# Revit family: HOSPIVAC G EVISA
name_source: partatom
category: Equipement de génie climatique
revit_build: Autodesk Revit 2018 (Build: 20170223_1515(x64)
units: mm (PartAtom-declared; Revit-internal decimal feet)

## family parameters
Basée sur le plan de construction = Non
Classification = Pompe
Cote de connecteur circulaire = Utiliser le diamètre
Couper avec des vides une fois chargée = Non
Partagée = Non
Point de calcul de pièce = Non
Toujours verticalement = Oui
Type d'élément = Normal

## types (11) — shared parameters
BRANCHEMENT_TERRE = Oui
COS_PHI = 0.9
DOUBLE_ALIMENTATION = Non
FREQUENCE = 50 Hz
Fabricant = MIL'S
Lien espace client = https://www.mils.fr
Modèle = HOSPIVAC G EVISA
NBR_POLES = 3
NEUTRE = Non
TENSION_ALIM = 400 V

## per-type parameters (varying)
| type | DEBIT_ASPI_VIDE | DEGAG_CALORIFIQUE(kJ/h) | DESCR_ALIM_ELECT | DESCR_ASPI | DESCR_REFOUL | DIAM_ASPI_VIDE | HAUT_PPE | NIVEAU_SONORE(dB(A)) | OFFSET_LARG_PPE | OFFSET_LONG_PPE | POIDS(Kg) | PROTECTION_ELECTRIQUE | PROTEC_ELECT | PUISS_APPARENTE | PUISS_ELECT | TYPE_PPE | TYPE_SOCLE |
| a - HOSPIVAC G E25 | 28.0 m³/h | 3100 | Alimentation électrique, 4G1.5mm² | Aspiration Vide ; 28 m³/h ; G 1" FEM | Refoulement Vide ; 28 m³/h ; G 1" FEM | 25 mm  [stored 0.082021 ft] | 150 mm  [stored 0.492126 ft] | 59 | 135 mm  [stored 0.442913 ft] | 92.5 mm  [stored 0.303478 ft] | 36 mm  [stored 0.11811 ft] | 4 A | Disjoncteur courbe D - 4 A | 833 VA | 1 kW | EVISA : b - E25.R | SOCLE HOSPIVAC G EVISA : SOCLE E25/40 |
| b - HOSPIVAC G E40 | 44.0 m³/h | 4548 | Alimentation électrique, 4G1.5mm² | Aspiration Vide ; 44 m³/h ; G 1" FEM | Refoulement Vide ; 44 m³/h ; G 1" FEM | 25 mm  [stored 0.082021 ft] | 150 mm  [stored 0.492126 ft] | 58 | 135 mm  [stored 0.442913 ft] | 92.5 mm  [stored 0.303478 ft] | 40 mm  [stored 0.131234 ft] | 4 A | Disjoncteur courbe D - 4 A | 1222 VA | 1 kW | EVISA : d - E40.R | SOCLE HOSPIVAC G EVISA : SOCLE E25/40 |
| c - HOSPIVAC G E65 | 68.0 m³/h | 6200 | Alimentation électrique, 4G1.5mm² | Aspiration Vide ; 68 m³/h ; G 1"1/4 FEM | Refoulement Vide ; 68 m³/h ; G 1"1/4 FEM | 32 mm  [stored 0.104987 ft] | 150 mm  [stored 0.492126 ft] | 67 | 122.5 mm  [stored 0.401903 ft] | 175.5 mm  [stored 0.575787 ft] | 70.5 mm | 6 A | Disjoncteur courbe D - 6 A | 1667 VA | 2 kW | EVISA : e - E65.R | SOCLE HOSPIVAC G EVISA : SOCLE E65/100 |
| e - HOSPIVAC G E150 | 132.0 m³/h | 12403 | Alimentation électrique, 4G2.5mm² | Aspiration Vide ; 132 m³/h ; G 2" FEM | Refoulement Vide ; 132 m³/h ; G 2" FEM | 50 mm  [stored 0.164042 ft] | 150 mm  [stored 0.492126 ft] | 69 | 171.3 mm  [stored 0.562008 ft] | 133 mm  [stored 0.436352 ft] | 166 mm  [stored 0.544619 ft] | 10 A | Disjoncteur courbe D - 10 A | 3333 VA | 3 kW | EVISA : g - E150.R | SOCLE HOSPIVAC G EVISA : SOCLE E150/200 |
| d - HOSPIVAC G E100 | 100.0 m³/h | 9095 | Alimentation électrique, 4G1.5mm² | Aspiration Vide ; 100 m³/h ; G 1"1/4 FEM | Refoulement Vide ; 100 m³/h ; G 1"1/4 FEM | 32 mm  [stored 0.104987 ft] | 150 mm  [stored 0.492126 ft] | 67 | 122.5 mm  [stored 0.401903 ft] | 175.5 mm  [stored 0.575787 ft] | 74.5 mm  [stored 0.244423 ft] | 10 A | Disjoncteur courbe D - 10 A | 2444 VA | 2 kW | EVISA : f - E100.R | SOCLE HOSPIVAC G EVISA : SOCLE E65/100 |
| f - HOSPIVAC G E200 | 200.0 m³/h | 16537 | Alimentation électrique, 4G2.5mm² | Aspiration Vide ; 200 m³/h ; G 2" FEM | Refoulement Vide ; 200 m³/h ; G 2" FEM | 50 mm  [stored 0.164042 ft] | 150 mm  [stored 0.492126 ft] | 71 | 171.3 mm  [stored 0.562008 ft] | 133 mm  [stored 0.436352 ft] | 155 mm  [stored 0.50853 ft] | 16 A | Disjoncteur courbe D - 16 A | 4444 VA | 4 kW | EVISA : h - E200.R | SOCLE HOSPIVAC G EVISA : SOCLE E150/200 |
| g - HOSPIVAC G E300 | 300.0 m³/h | 22738 | Alimentation électrique, 4G2.5mm² | Aspiration Vide ; 300 m³/h ; G 2" FEM | Refoulement Vide ; 300 m³/h ; G 2" FEM | 50 mm  [stored 0.164042 ft] | 150 mm  [stored 0.492126 ft] | 72 | 206 mm  [stored 0.675853 ft] | 160 mm  [stored 0.524934 ft] | 194 mm  [stored 0.636483 ft] | 20 A | Disjoncteur courbe D - 20 A | 6111 VA | 6 kW | EVISA : i - E300.R | SOCLE HOSPIVAC G EVISA : SOCLE E300 |
| h - HOSPIVAC G E350 | 360.0 m³/h | 31007 | Alimentation électrique, 4G4mm² | Aspiration Vide ; 360 m³/h ; BRIDE DN80 TARAUDÉ G3" | Refoulement Vide ; 360 m³/h ; G 3" FEM | 80 mm  [stored 0.262467 ft] | 200 mm  [stored 0.656168 ft] | 72 | 300 mm  [stored 0.984252 ft] | 190 mm  [stored 0.62336 ft] | 391 mm | 25 A | Disjoncteur courbe D - 25 A | 8333 VA | 8 kW | EVISA : j - E350.R | SOCLE HOSPIVAC G EVISA : SOCLE E350/600 |
| i - HOSPIVAC G E400 | 426.0 m³/h | 37208 | Alimentation électrique, 4G6mm² | Aspiration Vide ; 426 m³/h ; BRIDE DN80 TARAUDÉ G3" | Refoulement Vide ; 426 m³/h ; G 3" FEM | 80 mm  [stored 0.262467 ft] | 200 mm  [stored 0.656168 ft] | 72 | 300 mm  [stored 0.984252 ft] | 190 mm  [stored 0.62336 ft] | 436 mm  [stored 1.43045 ft] | 32 A | Disjoncteur courbe D - 32 A | 10000 VA | 9 kW | EVISA : k - E400.R | SOCLE HOSPIVAC G EVISA : SOCLE E350/600 |
| j - HOSPIVAC G E500 | 513.0 m³/h | 45476 | Alimentation électrique, 4G6mm² | Aspiration Vide ; 513 m³/h ; BRIDE DN80 TARAUDÉ G3" | Refoulement Vide ; 513 m³/h ; G 3" FEM | 80 mm  [stored 0.262467 ft] | 200 mm  [stored 0.656168 ft] | 73 | 300 mm  [stored 0.984252 ft] | 190 mm  [stored 0.62336 ft] | 490 mm  [stored 1.60761 ft] | 32 A | Disjoncteur courbe D - 32 A | 12222 VA | 11 kW | EVISA : l - E500.R | SOCLE HOSPIVAC G EVISA : SOCLE E350/600 |
| k - HOSPIVAC G E600 | 635.0 m³/h | 53745 | Alimentation électrique, 4G10mm² | Aspiration Vide ; 635 m³/h ; BRIDE DN80 TARAUDÉ G3" | Refoulement Vide ; 635 m³/h ; G 3" FEM | 80 mm  [stored 0.262467 ft] | 200 mm  [stored 0.656168 ft] | 74 | 300 mm  [stored 0.984252 ft] | 190 mm  [stored 0.62336 ft] | 558 mm | 40 A | Disjoncteur courbe D - 40 A | 14444 VA | 13 kW | EVISA : m - E600.R | SOCLE HOSPIVAC G EVISA : SOCLE E350/600 |

note: [stored X ft] marks values corroborated as IEEE doubles in the binary element streams (Revit-internal decimal feet)
